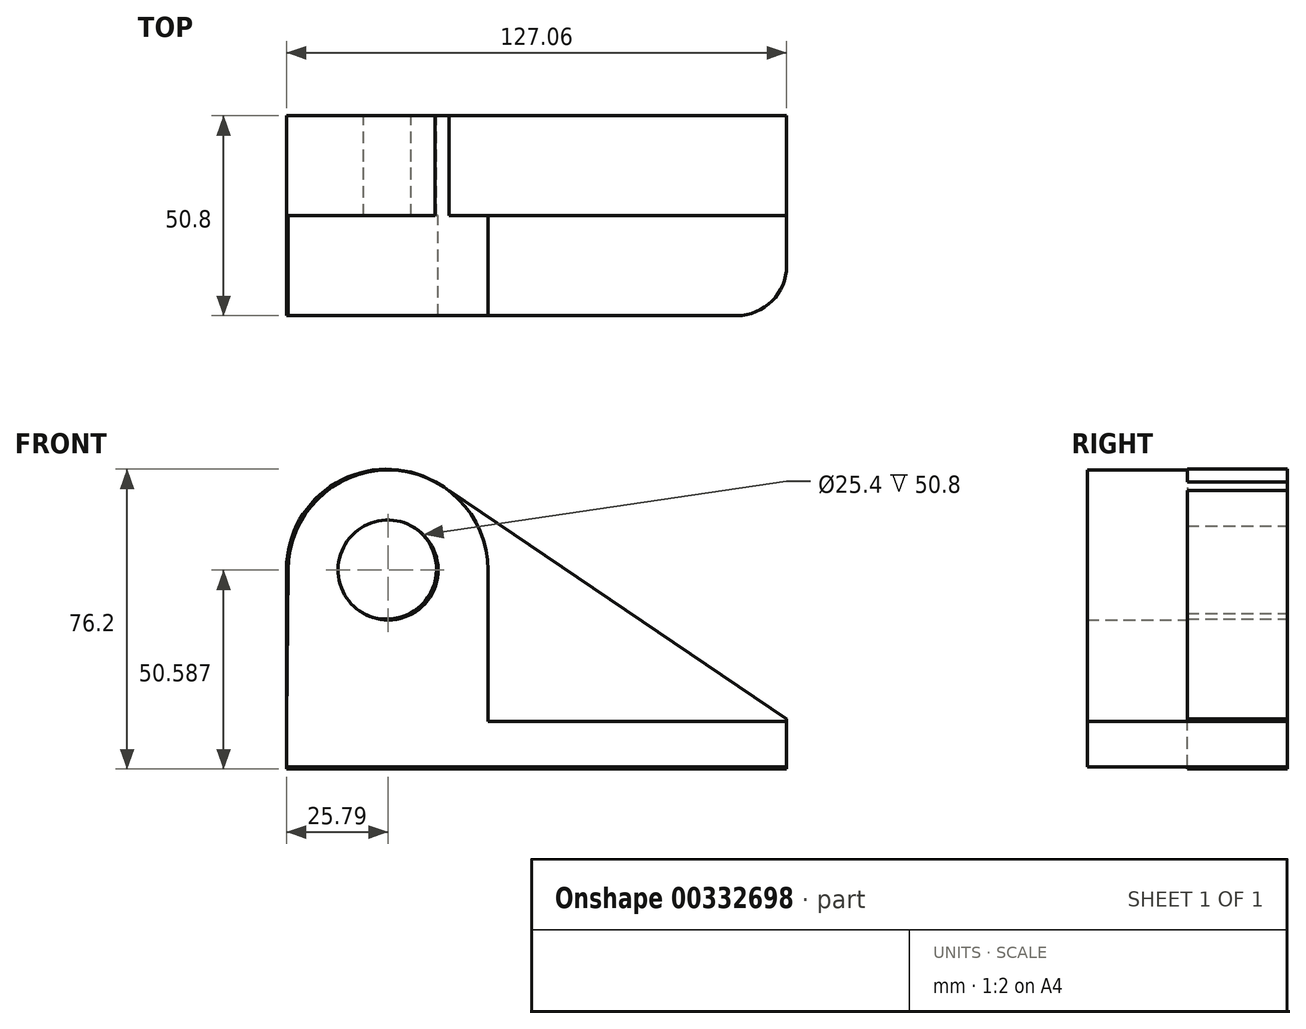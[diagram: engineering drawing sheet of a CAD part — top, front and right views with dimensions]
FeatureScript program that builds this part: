
annotation { "Feature Type Name" : "Feature", "Feature Type Description" : "" }
export const myFeature = defineFeature(function(context is Context, id is Id, definition is map)
    precondition{}
    {
        {
            var Q0;
            Q0=qCreatedBy(makeId("Front.planeOp"),FACE);
            var sketch = newSketch(context, id + "F0", { "sketchPlane" : qUnion([Q0])});
            skCircle(sketch, "E0", {"center": v(-38.36, 32.97) * mm, "radius": 12.7 * mm});
            skArc(sketch, "E1", {"start": v(-24.12, 54) * mm, "mid": v(-50.27, 55.4) * mm, "end": v(-63.76, 32.97) * mm});
            skLineSegment(sketch, "E2", {"start": v(-63.76, 32.97) * mm, "end": v(-63.76, -17.83) * mm});
            skLineSegment(sketch, "E3", {"start": v(-63.76, -17.83) * mm, "end": v(63.24, -17.83) * mm});
            skLineSegment(sketch, "E4", {"start": v(63.24, -17.83) * mm, "end": v(63.24, -5.13) * mm});
            skLineSegment(sketch, "E5", {"start": v(63.24, -5.13) * mm, "end": v(-24.12, 54) * mm});
            skSolve(sketch);
        }
        {
            var Q0;
            Q0 = qSketchRegion(id + "F0", true);
            extrude(context, id + "F1", {"entities" : qUnion([Q0]), "depth" : 25.4 * mm});
        }
        {
            var Q0;
            Q0=qCreatedBy(makeId("Front.planeOp"),FACE);
            var sketch = newSketch(context, id + "F2", { "sketchPlane" : qUnion([Q0])});
            skCircle(sketch, "E6", {"center": v(-37.97, 32.76) * mm, "radius": 12.7 * mm});
            skArc(sketch, "E7", {"start": v(-12.57, 32.76) * mm, "mid": v(-37.97, 58.16) * mm, "end": v(-63.37, 32.76) * mm});
            skLineSegment(sketch, "E8.bottom", {"start": v(63.3, -5.74) * mm, "end": v(-12.57, -5.74) * mm});
            skLineSegment(sketch, "E8.top", {"start": v(63.3, -17.23) * mm, "end": v(-63.7, -17.23) * mm});
            skLineSegment(sketch, "E8.left", {"start": v(63.3, -5.74) * mm, "end": v(63.3, -17.23) * mm});
            skLineSegment(sketch, "E8.right", {"start": v(-63.7, -5.74) * mm, "end": v(-63.7, -17.23) * mm});
            skLineSegment(sketch, "E9", {"start": v(-12.57, 32.76) * mm, "end": v(-12.57, -5.74) * mm});
            skLineSegment(sketch, "E10", {"start": v(-63.37, 32.76) * mm, "end": v(-63.7, -5.74) * mm});
            skSolve(sketch);
        }
        {
            var Q0;
            Q0=makeQuery(id+"F2.imprint","IMPRINT",FACE,{"disambiguationData":[TD([[makeQuery(id+"F2.imprint","IMPRINT",EDGE,{"derivedFrom":sQuery(id+"F2.wireOp",EDGE,"E6")}),-1.0]])]});
            extrude(context, id + "F3", {"entities" : qUnion([Q0]), "operationType" : NewBodyOperationType.ADD, "depth" : 50.8 * mm});
        }
        {
            var Q0;
            Q0=makeQuery(id+"F3.opExtrude","CAP_EDGE",EDGE,{"disambiguationData":[OSD([sQuery(id+"F2.wireOp",EDGE,"E8.left")])],"isStart":false});
            fillet(context, id + "F4", {"entities" : qUnion([Q0]), "radius" : 12.7 * mm, "tangentPropagation" : true, "allowEdgeOverflow" : false});
        }
    });
